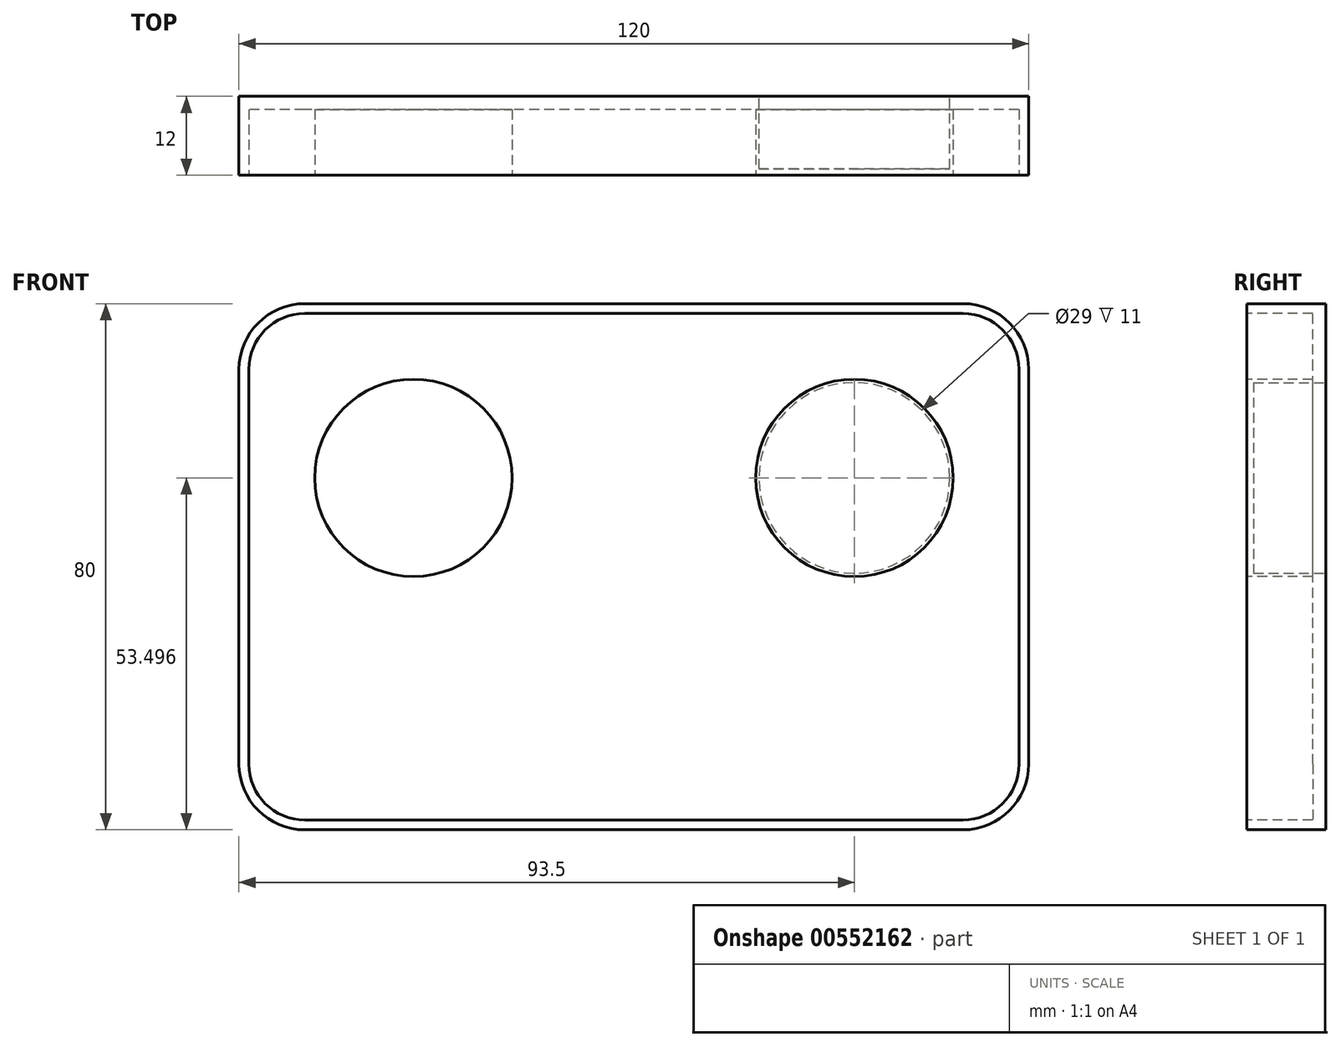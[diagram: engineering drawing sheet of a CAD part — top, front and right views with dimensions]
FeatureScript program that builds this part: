
annotation { "Feature Type Name" : "Feature", "Feature Type Description" : "" }
export const myFeature = defineFeature(function(context is Context, id is Id, definition is map)
    precondition{}
    {
        {
            var Q0;
            Q0=qCreatedBy(makeId("Front.planeOp"),FACE);
            var sketch = newSketch(context, id + "F0", { "sketchPlane" : qUnion([Q0])});
            skLineSegment(sketch, "E0.bottom", {"start": v(-77.5, -38.3) * mm, "end": v(22.5, -38.3) * mm});
            skLineSegment(sketch, "E0.top", {"start": v(-77.5, 41.7) * mm, "end": v(22.5, 41.7) * mm});
            skLineSegment(sketch, "E0.left", {"start": v(-87.5, -28.3) * mm, "end": v(-87.5, 31.7) * mm});
            skLineSegment(sketch, "E0.right", {"start": v(32.5, -28.3) * mm, "end": v(32.5, 31.7) * mm});
            skPoint(sketch, "E1.visualSharp", {"position": v(32.5, 41.7) * mm});
            skArc(sketch, "E1.filletArc", {"start": v(32.5, 31.7) * mm, "mid": v(29.57, 38.77) * mm, "end": v(22.5, 41.7) * mm});
            skPoint(sketch, "E2.visualSharp", {"position": v(-87.5, 41.7) * mm});
            skArc(sketch, "E2.filletArc", {"start": v(-77.5, 41.7) * mm, "mid": v(-84.57, 38.77) * mm, "end": v(-87.5, 31.7) * mm});
            skPoint(sketch, "E3.visualSharp", {"position": v(32.5, -38.3) * mm});
            skArc(sketch, "E3.filletArc", {"start": v(22.5, -38.3) * mm, "mid": v(29.57, -35.37) * mm, "end": v(32.5, -28.3) * mm});
            skPoint(sketch, "E4.visualSharp", {"position": v(-87.5, -38.3) * mm});
            skArc(sketch, "E4.filletArc", {"start": v(-87.5, -28.3) * mm, "mid": v(-84.57, -35.37) * mm, "end": v(-77.5, -38.3) * mm});
            skSolve(sketch);
        }
        {
            var Q0;
            Q0=makeQuery(id+"F0.imprint","IMPRINT",FACE,{"disambiguationData":[TD([[makeQuery(id+"F0.imprint","IMPRINT",EDGE,{"derivedFrom":sQuery(id+"F0.wireOp",EDGE,"E0.bottom")}),1.0]])]});
            extrude(context, id + "F1", {"entities" : qUnion([Q0]), "depth" : 12 * mm, "offsetDistance" : 25.4 * mm});
        }
        {
            var Q0;
            Q0=makeQuery(id+"F1.opExtrude","CAP_FACE",FACE,{"disambiguationData":[OSD([sQuery(id+"F0.wireOp",EDGE,"E0.bottom"),sQuery(id+"F0.wireOp",EDGE,"E0.top"),sQuery(id+"F0.wireOp",EDGE,"E0.left"),sQuery(id+"F0.wireOp",EDGE,"E0.right"),sQuery(id+"F0.wireOp",EDGE,"E1.filletArc"),sQuery(id+"F0.wireOp",EDGE,"E2.filletArc"),sQuery(id+"F0.wireOp",EDGE,"E3.filletArc"),sQuery(id+"F0.wireOp",EDGE,"E4.filletArc")])],"isStart":false});
            var sketch = newSketch(context, id + "F2", { "sketchPlane" : qUnion([Q0])});
            skCircle(sketch, "E5", {"center": v(-61, 15.2) * mm, "radius": 15 * mm});
            skArc(sketch, "E6.0", {"start": v(31, 31.7) * mm, "mid": v(28.51, 37.7) * mm, "end": v(22.5, 40.2) * mm});
            skLineSegment(sketch, "E6.1", {"start": v(31, -28.3) * mm, "end": v(31, 31.7) * mm});
            skLineSegment(sketch, "E6.2", {"start": v(22.5, 40.2) * mm, "end": v(-77.5, 40.2) * mm});
            skArc(sketch, "E6.3", {"start": v(22.5, -36.8) * mm, "mid": v(28.51, -34.31) * mm, "end": v(31, -28.3) * mm});
            skArc(sketch, "E6.4", {"start": v(-77.5, 40.2) * mm, "mid": v(-83.51, 37.7) * mm, "end": v(-86, 31.7) * mm});
            skLineSegment(sketch, "E6.5", {"start": v(-86, 31.7) * mm, "end": v(-86, -28.3) * mm});
            skArc(sketch, "E6.6", {"start": v(-86, -28.3) * mm, "mid": v(-83.51, -34.31) * mm, "end": v(-77.5, -36.8) * mm});
            skLineSegment(sketch, "E6.7", {"start": v(-77.5, -36.8) * mm, "end": v(22.5, -36.8) * mm});
            skCircle(sketch, "E7", {"center": v(6, 15.2) * mm, "radius": 15 * mm});
            skSolve(sketch);
        }
        {
            var Q0;
            Q0 = qSketchRegion(id + "F2", true);
            extrude(context, id + "F3", {"entities" : qUnion([Q0]), "operationType" : NewBodyOperationType.REMOVE, "oppositeDirection" : true, "depth" : 10 * mm, "offsetDistance" : 25 * mm});
        }
        {
            var Q0;
            Q0=makeQuery(id+"F1.opExtrude","CAP_FACE",FACE,{"disambiguationData":[OSD([sQuery(id+"F0.wireOp",EDGE,"E0.bottom"),sQuery(id+"F0.wireOp",EDGE,"E0.top"),sQuery(id+"F0.wireOp",EDGE,"E0.left"),sQuery(id+"F0.wireOp",EDGE,"E0.right"),sQuery(id+"F0.wireOp",EDGE,"E1.filletArc"),sQuery(id+"F0.wireOp",EDGE,"E2.filletArc"),sQuery(id+"F0.wireOp",EDGE,"E3.filletArc"),sQuery(id+"F0.wireOp",EDGE,"E4.filletArc")])],"isStart":true});
            var sketch = newSketch(context, id + "F4", { "sketchPlane" : qUnion([Q0])});
            skCircle(sketch, "E8", {"center": v(-6, 15.2) * mm, "radius": 14.5 * mm});
            skSolve(sketch);
        }
        {
            var Q0;
            Q0 = qSketchRegion(id + "F4", true);
            extrude(context, id + "F5", {"entities" : qUnion([Q0]), "operationType" : NewBodyOperationType.REMOVE, "oppositeDirection" : true, "depth" : 11 * mm, "offsetDistance" : 25 * mm});
        }
    });
